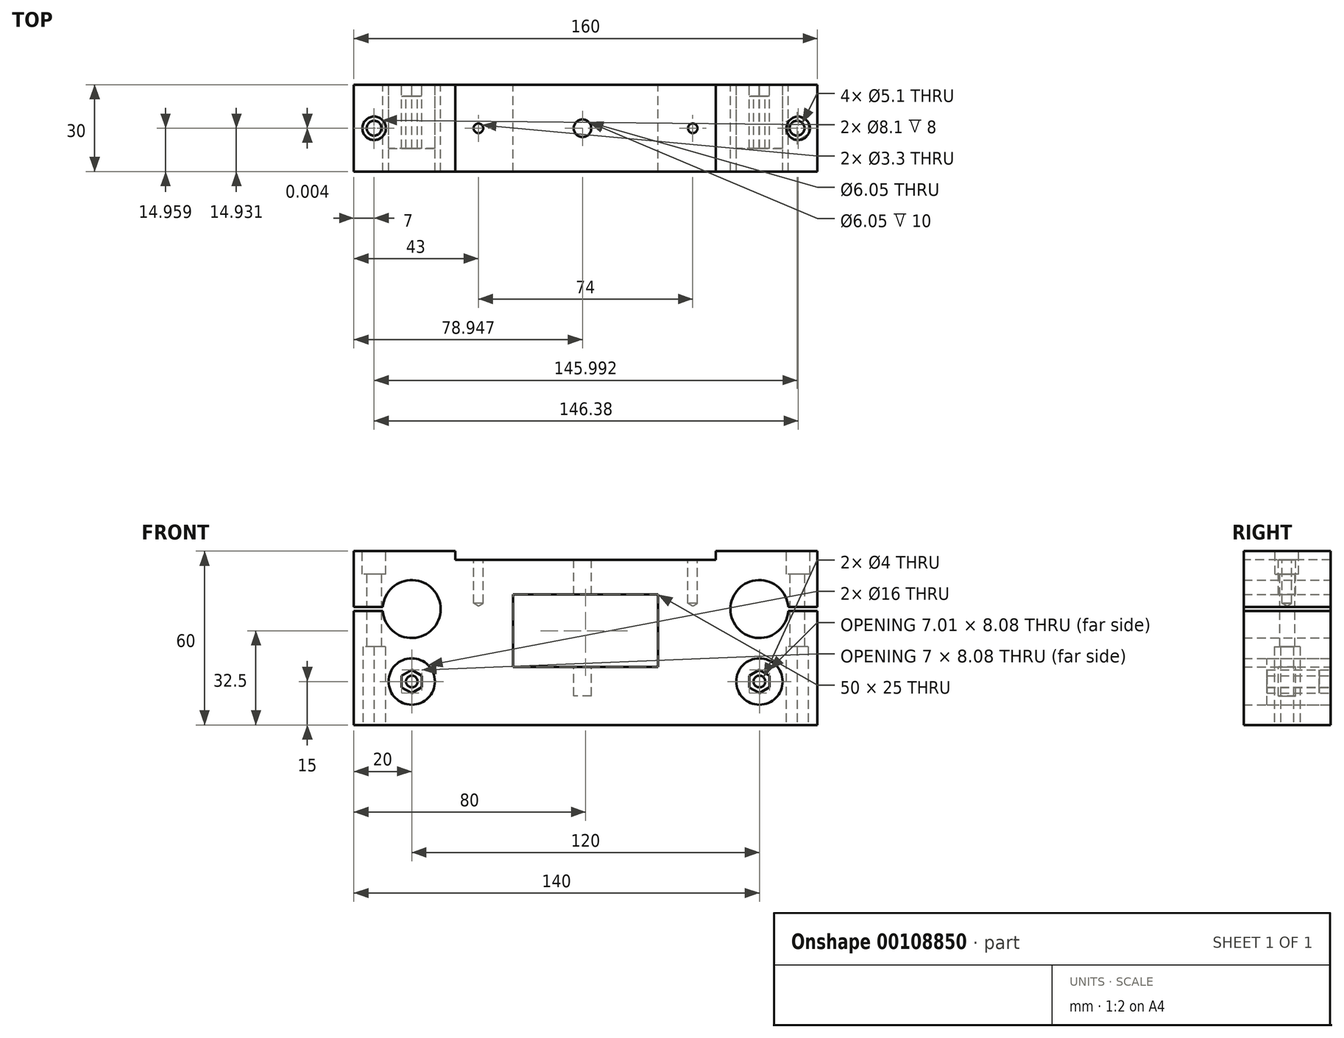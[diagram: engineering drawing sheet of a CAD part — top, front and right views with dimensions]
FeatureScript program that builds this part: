
annotation { "Feature Type Name" : "Feature", "Feature Type Description" : "" }
export const myFeature = defineFeature(function(context is Context, id is Id, definition is map)
    precondition{}
    {
        {
            var Q0;
            Q0=qCreatedBy(makeId("Front.planeOp"),FACE);
            var sketch = newSketch(context, id + "F0", { "sketchPlane" : qUnion([Q0])});
            skLineSegment(sketch, "E0.bottom", {"start": v(-20, 0) * mm, "end": v(140, 0) * mm});
            skLineSegment(sketch, "E0.top", {"start": v(-20, 60) * mm, "end": v(140, 60) * mm});
            skLineSegment(sketch, "E0.left", {"start": v(-20, 0) * mm, "end": v(-20, 60) * mm});
            skLineSegment(sketch, "E0.right", {"start": v(140, 0) * mm, "end": v(140, 60) * mm});
            skLineSegment(sketch, "E1", {"start": v(-32.3, 40) * mm, "end": v(141.24, 40) * mm, "construction": true});
            skLineSegment(sketch, "E2", {"start": v(60, 68.67) * mm, "end": v(60, -11.64) * mm, "construction": true});
            skLineSegment(sketch, "E3", {"start": v(0, 64.15) * mm, "end": v(0, -12.13) * mm, "construction": true});
            skLineSegment(sketch, "E4", {"start": v(120, 65.28) * mm, "end": v(120, -11.74) * mm, "construction": true});
            skCircle(sketch, "E5", {"center": v(0, 40) * mm, "radius": 10 * mm});
            skCircle(sketch, "E6", {"center": v(120, 40) * mm, "radius": 10 * mm});
            skLineSegment(sketch, "E7", {"start": v(0, 50) * mm, "end": v(-26.2, 50) * mm, "construction": true});
            skLineSegment(sketch, "E8.bottom", {"start": v(-20, 40) * mm, "end": v(-7.94, 40) * mm});
            skLineSegment(sketch, "E8.top", {"start": v(-20, 40.7) * mm, "end": v(-7.94, 40.7) * mm});
            skLineSegment(sketch, "E8.left", {"start": v(-20, 40) * mm, "end": v(-20, 40.7) * mm});
            skLineSegment(sketch, "E8.right", {"start": v(-7.94, 40) * mm, "end": v(-7.94, 40.7) * mm});
            skLineSegment(sketch, "E9.top", {"start": v(-20, 39.3) * mm, "end": v(-7.94, 39.3) * mm});
            skLineSegment(sketch, "E9.left", {"start": v(-20, 40) * mm, "end": v(-20, 39.3) * mm});
            skLineSegment(sketch, "E9.right", {"start": v(-7.94, 40) * mm, "end": v(-7.94, 39.3) * mm});
            skLineSegment(sketch, "E10.bottom", {"start": v(140, 40) * mm, "end": v(115.05, 40) * mm});
            skLineSegment(sketch, "E10.top", {"start": v(140, 40.7) * mm, "end": v(115.05, 40.7) * mm});
            skLineSegment(sketch, "E10.left", {"start": v(140, 40) * mm, "end": v(140, 40.7) * mm});
            skLineSegment(sketch, "E10.right", {"start": v(115.05, 40) * mm, "end": v(115.05, 40.7) * mm});
            skLineSegment(sketch, "E11.top", {"start": v(140, 39.3) * mm, "end": v(115.05, 39.3) * mm});
            skLineSegment(sketch, "E11.left", {"start": v(140, 40) * mm, "end": v(140, 39.3) * mm});
            skLineSegment(sketch, "E11.right", {"start": v(115.05, 40) * mm, "end": v(115.05, 39.3) * mm});
            skLineSegment(sketch, "E12.bottom", {"start": v(35, 20) * mm, "end": v(85, 20) * mm});
            skLineSegment(sketch, "E12.top", {"start": v(35, 45) * mm, "end": v(85, 45) * mm});
            skLineSegment(sketch, "E12.left", {"start": v(35, 20) * mm, "end": v(35, 45) * mm});
            skLineSegment(sketch, "E12.right", {"start": v(85, 20) * mm, "end": v(85, 45) * mm});
            skLineSegment(sketch, "E13", {"start": v(-26.39, 15) * mm, "end": v(147.53, 15) * mm, "construction": true});
            skCircle(sketch, "E14", {"center": v(0, 15) * mm, "radius": 8 * mm});
            skCircle(sketch, "E15", {"center": v(0, 15) * mm, "radius": 2 * mm});
            skCircle(sketch, "E16", {"center": v(120, 15) * mm, "radius": 8 * mm});
            skCircle(sketch, "E17", {"center": v(120, 15) * mm, "radius": 2 * mm});
            skCircle(sketch, "E18.cCircle", {"center": v(120, 15) * mm, "radius": 3.5 * mm, "construction": true});
            skLineSegment(sketch, "E18.0", {"start": v(119.99, 19.04) * mm, "end": v(123.5, 17.03) * mm});
            skLineSegment(sketch, "E18.1", {"start": v(123.5, 17.03) * mm, "end": v(123.5, 13) * mm});
            skLineSegment(sketch, "E18.2", {"start": v(123.5, 13) * mm, "end": v(120.01, 10.96) * mm});
            skLineSegment(sketch, "E18.3", {"start": v(120.01, 10.96) * mm, "end": v(116.5, 12.97) * mm});
            skLineSegment(sketch, "E18.4", {"start": v(116.5, 12.97) * mm, "end": v(116.5, 17) * mm});
            skLineSegment(sketch, "E18.5", {"start": v(116.5, 17) * mm, "end": v(119.99, 19.04) * mm});
            skPoint(sketch, "E18.0.midPoint", {"position": v(121.74, 18.04) * mm});
            skCircle(sketch, "E19.cCircle", {"center": v(0, 15) * mm, "radius": 3.5 * mm, "construction": true});
            skLineSegment(sketch, "E19.0", {"start": v(-3.5, 17.02) * mm, "end": v(0, 19.04) * mm});
            skLineSegment(sketch, "E19.1", {"start": v(0, 19.04) * mm, "end": v(3.5, 17.02) * mm});
            skLineSegment(sketch, "E19.2", {"start": v(3.5, 17.02) * mm, "end": v(3.5, 12.98) * mm});
            skLineSegment(sketch, "E19.3", {"start": v(3.5, 12.98) * mm, "end": v(0, 10.96) * mm});
            skLineSegment(sketch, "E19.4", {"start": v(0, 10.96) * mm, "end": v(-3.5, 12.98) * mm});
            skLineSegment(sketch, "E19.5", {"start": v(-3.5, 12.98) * mm, "end": v(-3.5, 17.02) * mm});
            skPoint(sketch, "E19.0.midPoint", {"position": v(-1.75, 18.03) * mm});
            skSolve(sketch);
        }
        {
            var Q0;
            {var subQ12=sQuery(id+"F0.wireOp",EDGE,"E0.bottom");Q0=makeQuery(id+"F0.imprint","IMPRINT",FACE,{"disambiguationData":[TD([[makeQuery(id+"F0.imprint","IMPRINT",EDGE,{"derivedFrom":subQ12}),1.0]])]});}
            extrude(context, id + "F1", {"entities" : qUnion([Q0]), "depth" : 30 * mm});
        }
        {
            var Q0;
            Q0=qCreatedBy(makeId("Top.planeOp"),FACE);
            var sketch = newSketch(context, id + "F2", { "sketchPlane" : qUnion([Q0])});
            skLineSegment(sketch, "E20", {"start": v(33.95, 0) * mm, "end": v(33.95, -38.86) * mm, "construction": true});
            skLineSegment(sketch, "E21", {"start": v(83.95, 0) * mm, "end": v(83.95, -38.12) * mm, "construction": true});
            skLineSegment(sketch, "E22", {"start": v(-24.4, 0) * mm, "end": v(144.16, 0) * mm});
            skLineSegment(sketch, "E23", {"start": v(-13, 7.6) * mm, "end": v(-13, -37.06) * mm, "construction": true});
            skLineSegment(sketch, "E24", {"start": v(133, 6.36) * mm, "end": v(133, -40.54) * mm, "construction": true});
            skLineSegment(sketch, "E25", {"start": v(-28.1, -15.04) * mm, "end": v(140.96, -15.04) * mm, "construction": true});
            skCircle(sketch, "E26.cCircle", {"center": v(-13, -15.04) * mm, "radius": 4.45 * mm, "construction": true});
            skLineSegment(sketch, "E26.0", {"start": v(-16.85, -17.27) * mm, "end": v(-16.85, -12.82) * mm});
            skLineSegment(sketch, "E26.1", {"start": v(-16.85, -12.82) * mm, "end": v(-13, -10.6) * mm});
            skLineSegment(sketch, "E26.2", {"start": v(-13, -10.6) * mm, "end": v(-9.15, -12.82) * mm});
            skLineSegment(sketch, "E26.3", {"start": v(-9.15, -12.82) * mm, "end": v(-9.15, -17.27) * mm});
            skLineSegment(sketch, "E26.4", {"start": v(-9.15, -17.27) * mm, "end": v(-13, -19.5) * mm});
            skLineSegment(sketch, "E26.5", {"start": v(-13, -19.5) * mm, "end": v(-16.85, -17.27) * mm});
            skCircle(sketch, "E27.cCircle", {"center": v(133, -15.04) * mm, "radius": 4.45 * mm, "construction": true});
            skLineSegment(sketch, "E27.0", {"start": v(129.15, -17.27) * mm, "end": v(129.15, -12.82) * mm});
            skLineSegment(sketch, "E27.1", {"start": v(129.15, -12.82) * mm, "end": v(133, -10.6) * mm});
            skLineSegment(sketch, "E27.2", {"start": v(133, -10.6) * mm, "end": v(136.85, -12.82) * mm});
            skLineSegment(sketch, "E27.3", {"start": v(136.85, -12.82) * mm, "end": v(136.85, -17.27) * mm});
            skLineSegment(sketch, "E27.4", {"start": v(136.85, -17.27) * mm, "end": v(133, -19.5) * mm});
            skLineSegment(sketch, "E27.5", {"start": v(133, -19.5) * mm, "end": v(129.15, -17.27) * mm});
            skSolve(sketch);
        }
        {
            var Q0;
            Q0=makeQuery(id+"F2.imprint","IMPRINT",FACE,{"disambiguationData":[TD([[makeQuery(id+"F2.imprint","IMPRINT",EDGE,{"derivedFrom":sQuery(id+"F2.wireOp",EDGE,"E27.0")}),-1.0]])]});
            var Q1;
            Q1=makeQuery(id+"F2.imprint","IMPRINT",FACE,{"disambiguationData":[TD([[makeQuery(id+"F2.imprint","IMPRINT",EDGE,{"derivedFrom":sQuery(id+"F2.wireOp",EDGE,"E26.0")}),-1.0]])]});
            extrude(context, id + "F3", {"entities" : qUnion([Q0, Q1]), "operationType" : NewBodyOperationType.REMOVE, "depth" : 27 * mm});
        }
        {
            var Q0;
            Q0=qCreatedBy(makeId("Top.planeOp"),FACE);
            var sketch = newSketch(context, id + "F4", { "sketchPlane" : qUnion([Q0])});
            skCircle(sketch, "E28", {"center": v(-13, -15.04) * mm, "radius": 4.05 * mm});
            skCircle(sketch, "E29", {"center": v(-13, -15.04) * mm, "radius": 2.55 * mm});
            skCircle(sketch, "E30", {"center": v(133, -15.04) * mm, "radius": 4.05 * mm});
            skCircle(sketch, "E31", {"center": v(133, -15.04) * mm, "radius": 2.55 * mm});
            skSolve(sketch);
        }
        {
            var Q0;
            Q0=makeQuery(id+"F4.imprint","IMPRINT",FACE,{"disambiguationData":[TD([[makeQuery(id+"F4.imprint","IMPRINT",EDGE,{"derivedFrom":sQuery(id+"F4.wireOp",EDGE,"E31")}),1.0]])]});
            var Q1;
            Q1=makeQuery(id+"F4.imprint","IMPRINT",FACE,{"disambiguationData":[TD([[makeQuery(id+"F4.imprint","IMPRINT",EDGE,{"derivedFrom":sQuery(id+"F4.wireOp",EDGE,"E29")}),1.0]])]});
            extrude(context, id + "F5", {"entities" : qUnion([Q0, Q1]), "operationType" : NewBodyOperationType.REMOVE, "endBound" : BoundingType.THROUGH_ALL, "depth" : 25 * mm});
        }
        {
            var Q0;
            Q0=makeQuery(id+"F4.imprint","IMPRINT",FACE,{"disambiguationData":[TD([[makeQuery(id+"F4.imprint","IMPRINT",EDGE,{"derivedFrom":sQuery(id+"F4.wireOp",EDGE,"E28")}),1.0]])]});
            var Q1;
            Q1=makeQuery(id+"F4.imprint","IMPRINT",FACE,{"disambiguationData":[TD([[makeQuery(id+"F4.imprint","IMPRINT",EDGE,{"derivedFrom":sQuery(id+"F4.wireOp",EDGE,"E30")}),1.0]])]});
            var Q2;
            Q2=sQuery(id+"F4.wireOp",EDGE,"E28");
            extrude(context, id + "F6", {"entities" : qUnion([Q0, Q1]), "operationType" : NewBodyOperationType.REMOVE, "surfaceEntities" : qUnion([Q2]), "oppositeDirection" : true, "depth" : 10 * mm});
        }
        {
            var Q0;
            Q0=makeQuery(id+"F1.opExtrude","SWEPT_FACE",FACE,{"disambiguationData":[OSD([sQuery(id+"F0.wireOp",EDGE,"E0.top")])]});
            cPlane(context, id + "F7", {"entities" : qUnion([Q0]), "cplaneType" : CPlaneType.OFFSET, "offset" : 0 * mm, "width" : 150 * mm, "height" : 150 * mm});
        }
        {
            var Q0;
            Q0=qCreatedBy(id+"F7.planeOp",FACE);
            var sketch = newSketch(context, id + "F8", { "sketchPlane" : qUnion([Q0])});
            skLineSegment(sketch, "E32", {"start": v(-28.54, -15.07) * mm, "end": v(153.78, -15.07) * mm, "construction": true});
            skLineSegment(sketch, "E33", {"start": v(133.38, 6.08) * mm, "end": v(133.38, -40.71) * mm, "construction": true});
            skLineSegment(sketch, "E34", {"start": v(-13, 7.77) * mm, "end": v(-13, -37.72) * mm, "construction": true});
            skLineSegment(sketch, "E35", {"start": v(33.95, -39.02) * mm, "end": v(33.95, 4.96) * mm, "construction": true});
            skLineSegment(sketch, "E36", {"start": v(83.95, -38.14) * mm, "end": v(83.95, 6.2) * mm, "construction": true});
            skLineSegment(sketch, "E37", {"start": v(58.95, 0) * mm, "end": v(58.95, -35.38) * mm, "construction": true});
            skPoint(sketch, "E38", {"position": v(58.95, -15.07) * mm});
            skPoint(sketch, "E39", {"position": v(-13, -15.07) * mm});
            skPoint(sketch, "E40", {"position": v(133.38, -15.07) * mm});
            skPoint(sketch, "E41", {"position": v(33.95, 2.05) * mm});
            skCircle(sketch, "E42", {"center": v(58.95, -15.07) * mm, "radius": 3.02 * mm});
            skCircle(sketch, "E43", {"center": v(-13, -15.07) * mm, "radius": 4.05 * mm});
            skCircle(sketch, "E44", {"center": v(133.38, -15.07) * mm, "radius": 4.05 * mm});
            skLineSegment(sketch, "E45", {"start": v(41.3, -6.51) * mm, "end": v(41.3, -24.38) * mm, "construction": true});
            skLineSegment(sketch, "E46.bottom", {"start": v(15, 0) * mm, "end": v(105, 0) * mm});
            skLineSegment(sketch, "E46.top", {"start": v(15, -31.8) * mm, "end": v(105, -31.8) * mm});
            skLineSegment(sketch, "E46.left", {"start": v(15, 0) * mm, "end": v(15, -31.8) * mm});
            skLineSegment(sketch, "E46.right", {"start": v(105, 0) * mm, "end": v(105, -31.8) * mm});
            skLineSegment(sketch, "E47", {"start": v(23, -10.04) * mm, "end": v(23, -22.62) * mm, "construction": true});
            skLineSegment(sketch, "E48", {"start": v(97, -9.6) * mm, "end": v(97, -22.02) * mm, "construction": true});
            skPoint(sketch, "E49", {"position": v(23, -15.07) * mm});
            skPoint(sketch, "E50", {"position": v(97, -15.07) * mm});
            skSolve(sketch);
        }
        {
            var Q0;
            Q0=makeQuery(id+"F8.imprint","IMPRINT",FACE,{"disambiguationData":[TD([[makeQuery(id+"F8.imprint","IMPRINT",EDGE,{"derivedFrom":sQuery(id+"F8.wireOp",EDGE,"E43")}),1.0]])]});
            var Q1;
            Q1=makeQuery(id+"F8.imprint","IMPRINT",FACE,{"disambiguationData":[TD([[makeQuery(id+"F8.imprint","IMPRINT",EDGE,{"derivedFrom":sQuery(id+"F8.wireOp",EDGE,"E44")}),1.0]])]});
            extrude(context, id + "F9", {"entities" : qUnion([Q0, Q1]), "operationType" : NewBodyOperationType.REMOVE, "oppositeDirection" : true, "depth" : 8 * mm});
        }
        {
            var Q0;
            Q0=makeQuery(id+"F8.imprint","IMPRINT",FACE,{"disambiguationData":[TD([[makeQuery(id+"F8.imprint","IMPRINT",EDGE,{"derivedFrom":sQuery(id+"F8.wireOp",EDGE,"E42")}),1.0]])]});
            extrude(context, id + "F10", {"entities" : qUnion([Q0]), "operationType" : NewBodyOperationType.REMOVE, "oppositeDirection" : true, "depth" : 50 * mm});
        }
        {
            var Q0;
            Q0=makeQuery(id+"F8.imprint","IMPRINT",FACE,{"disambiguationData":[TD([[makeQuery(id+"F8.imprint","IMPRINT",EDGE,{"derivedFrom":sQuery(id+"F8.wireOp",EDGE,"E42")}),-1.0]])]});
            extrude(context, id + "F11", {"entities" : qUnion([Q0]), "operationType" : NewBodyOperationType.REMOVE, "oppositeDirection" : true, "depth" : 3 * mm});
        }
        {
            var Q0;
            Q0=sQuery(id+"F8.wireOp",VERTEX,"E49");
            var Q1;
            Q1=sQuery(id+"F8.wireOp",VERTEX,"E50");
            var Q2;
            Q2=makeQuery(id+"F1.opExtrude","SWEPT_BODY",BODY,{"disambiguationData":[OSD([sQuery(id+"F0.wireOp",EDGE,"E0.bottom"),sQuery(id+"F0.wireOp",EDGE,"E0.top"),sQuery(id+"F0.wireOp",EDGE,"E0.left"),sQuery(id+"F0.wireOp",EDGE,"E0.right"),sQuery(id+"F0.wireOp",EDGE,"E5"),sQuery(id+"F0.wireOp",EDGE,"E6"),sQuery(id+"F0.wireOp",EDGE,"E8.top"),sQuery(id+"F0.wireOp",EDGE,"E9.top"),sQuery(id+"F0.wireOp",EDGE,"E10.top"),sQuery(id+"F0.wireOp",EDGE,"E11.top"),sQuery(id+"F0.wireOp",EDGE,"E12.bottom"),sQuery(id+"F0.wireOp",EDGE,"E12.top"),sQuery(id+"F0.wireOp",EDGE,"E12.left"),sQuery(id+"F0.wireOp",EDGE,"E12.right")])]});
            hole(context, id + "F12", {"style" : HoleStyle.SIMPLE, "endStyle" : HoleEndStyle.BLIND, "standardTappedOrClearance" : lookupTablePath({ "standard" : "ISO", "fit" : "Normal", "size" : "M3", "type" : "Clearance" }), "standardBlindInLast" : lookupTablePath({ "fit" : "Standard", "standard" : "ISO", "size" : "M3", "type" : "Clearance" }), "holeDiameter" : 3.3 * mm, "holeDepth" : 18 * mm, "startFromSketch" : true, "locations" : qUnion([Q0, Q1]), "scope" : qUnion([Q2])});
        }
        {
            var Q0;
            Q0=makeQuery(id+"F0.imprint","IMPRINT",FACE,{"disambiguationData":[TD([[makeQuery(id+"F0.imprint","IMPRINT",EDGE,{"derivedFrom":sQuery(id+"F0.wireOp",EDGE,"E15")}),-1.0]])]});
            var Q1;
            Q1=makeQuery(id+"F0.imprint","IMPRINT",FACE,{"disambiguationData":[TD([[makeQuery(id+"F0.imprint","IMPRINT",EDGE,{"derivedFrom":sQuery(id+"F0.wireOp",EDGE,"E17")}),-1.0]])]});
            extrude(context, id + "F13", {"entities" : qUnion([Q0, Q1]), "operationType" : NewBodyOperationType.REMOVE, "depth" : 4 * mm});
        }
        {
            var Q0;
            Q0=makeQuery(id+"F0.imprint","IMPRINT",FACE,{"disambiguationData":[TD([[makeQuery(id+"F0.imprint","IMPRINT",EDGE,{"derivedFrom":sQuery(id+"F0.wireOp",EDGE,"E16")}),1.0]])]});
            var Q1;
            Q1=makeQuery(id+"F0.imprint","IMPRINT",FACE,{"disambiguationData":[TD([[makeQuery(id+"F0.imprint","IMPRINT",EDGE,{"derivedFrom":sQuery(id+"F0.wireOp",EDGE,"E14")}),1.0]])]});
            extrude(context, id + "F14", {"entities" : qUnion([Q0, Q1]), "depth" : 22 * mm});
        }
        {
            var Q0;
            Q0=makeQuery(id+"F0.imprint","IMPRINT",FACE,{"disambiguationData":[TD([[makeQuery(id+"F0.imprint","IMPRINT",EDGE,{"derivedFrom":sQuery(id+"F0.wireOp",EDGE,"E17")}),-1.0]])]});
            var Q1;
            Q1=makeQuery(id+"F0.imprint","IMPRINT",FACE,{"disambiguationData":[TD([[makeQuery(id+"F0.imprint","IMPRINT",EDGE,{"derivedFrom":sQuery(id+"F0.wireOp",EDGE,"E15")}),-1.0]])]});
            extrude(context, id + "F15", {"entities" : qUnion([Q0, Q1]), "depth" : 22 * mm});
        }
        {
            var Q0;
            Q0=makeQuery(id+"F0.imprint","IMPRINT",FACE,{"disambiguationData":[TD([[makeQuery(id+"F0.imprint","IMPRINT",EDGE,{"derivedFrom":sQuery(id+"F0.wireOp",EDGE,"E15")}),-1.0]])]});
            var Q1;
            Q1=makeQuery(id+"F0.imprint","IMPRINT",FACE,{"disambiguationData":[TD([[makeQuery(id+"F0.imprint","IMPRINT",EDGE,{"derivedFrom":sQuery(id+"F0.wireOp",EDGE,"E17")}),-1.0]])]});
            extrude(context, id + "F16", {"entities" : qUnion([Q0, Q1]), "operationType" : NewBodyOperationType.REMOVE, "depth" : 4 * mm});
        }
    });
